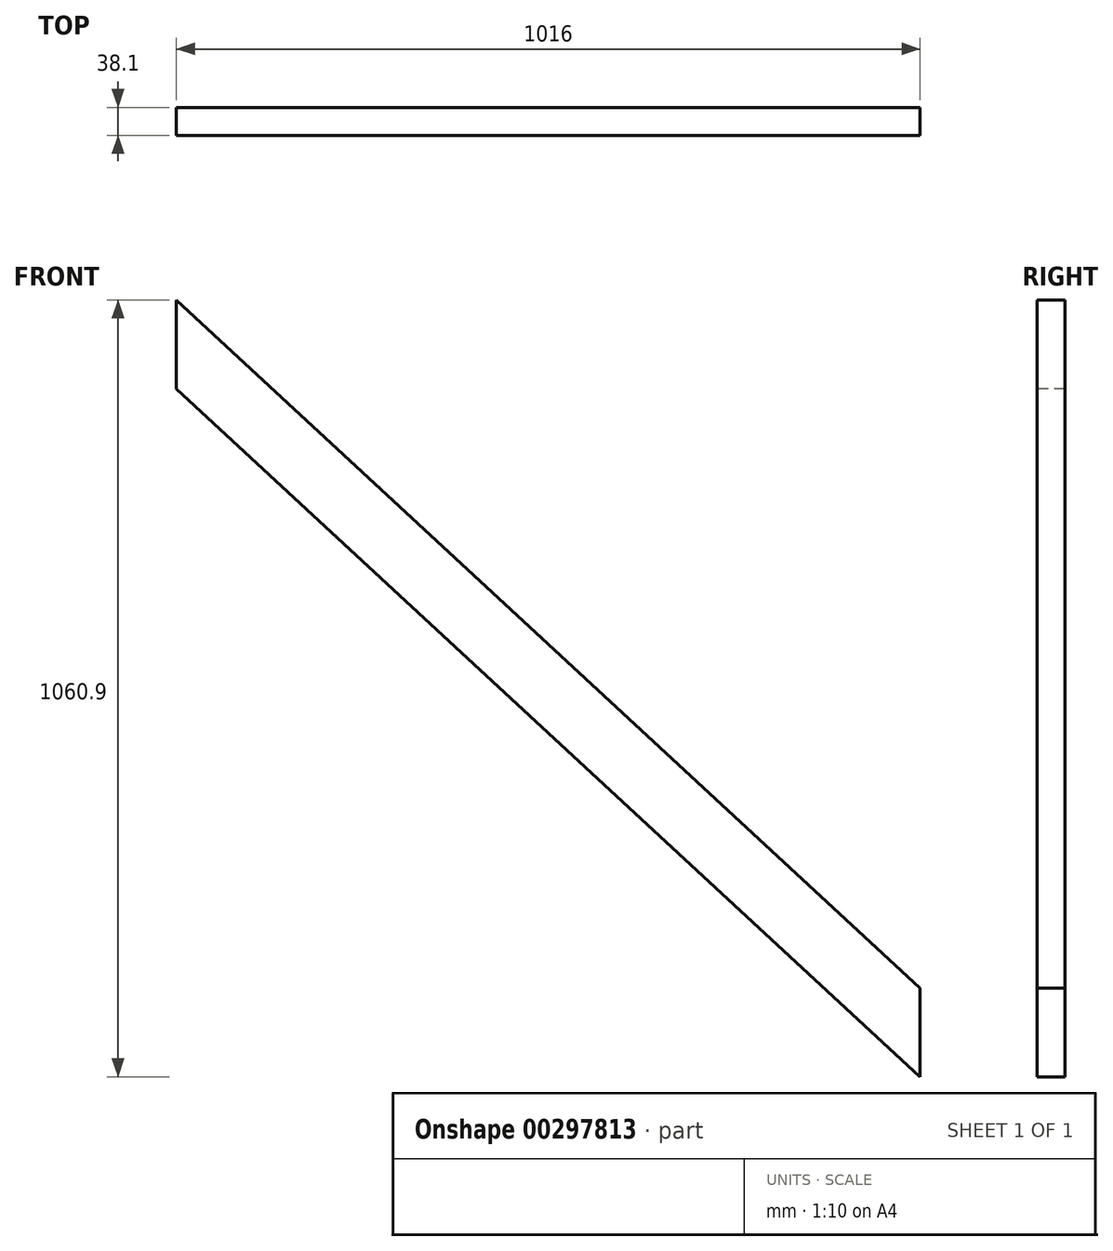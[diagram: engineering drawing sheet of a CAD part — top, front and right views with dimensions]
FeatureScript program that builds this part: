
annotation { "Feature Type Name" : "Feature", "Feature Type Description" : "" }
export const myFeature = defineFeature(function(context is Context, id is Id, definition is map)
    precondition{}
    {
        {
            var Q0;
            Q0=qCreatedBy(makeId("Front.planeOp"),FACE);
            var sketch = newSketch(context, id + "F0", { "sketchPlane" : qUnion([Q0])});
            skLineSegment(sketch, "E0.left", {"start": v(0, 0) * mm, "end": v(0, -121.1) * mm});
            skLineSegment(sketch, "E1", {"start": v(0, 0) * mm, "end": v(1016, -939.8) * mm});
            skLineSegment(sketch, "E2", {"start": v(1016, -1060.9) * mm, "end": v(0, -121.1) * mm});
            skLineSegment(sketch, "E3", {"start": v(1016, -939.8) * mm, "end": v(1016, -1060.9) * mm});
            skSolve(sketch);
        }
        {
            var Q0;
            Q0=makeQuery(id+"F0.imprint","IMPRINT",FACE,{"disambiguationData":[TD([[makeQuery(id+"F0.imprint","IMPRINT",EDGE,{"derivedFrom":sQuery(id+"F0.wireOp",EDGE,"E0.top")}),1.0]])]});
            var Q1;
            Q1=makeQuery(id+"F0.imprint","IMPRINT",FACE,{"disambiguationData":[TD([[makeQuery(id+"F0.imprint","IMPRINT",EDGE,{"derivedFrom":sQuery(id+"F0.wireOp",EDGE,"E0.left")}),1.0]])]});
            extrude(context, id + "F1", {"entities" : qUnion([Q0, Q1]), "oppositeDirection" : true, "depth" : 38.1 * mm});
        }
    });
